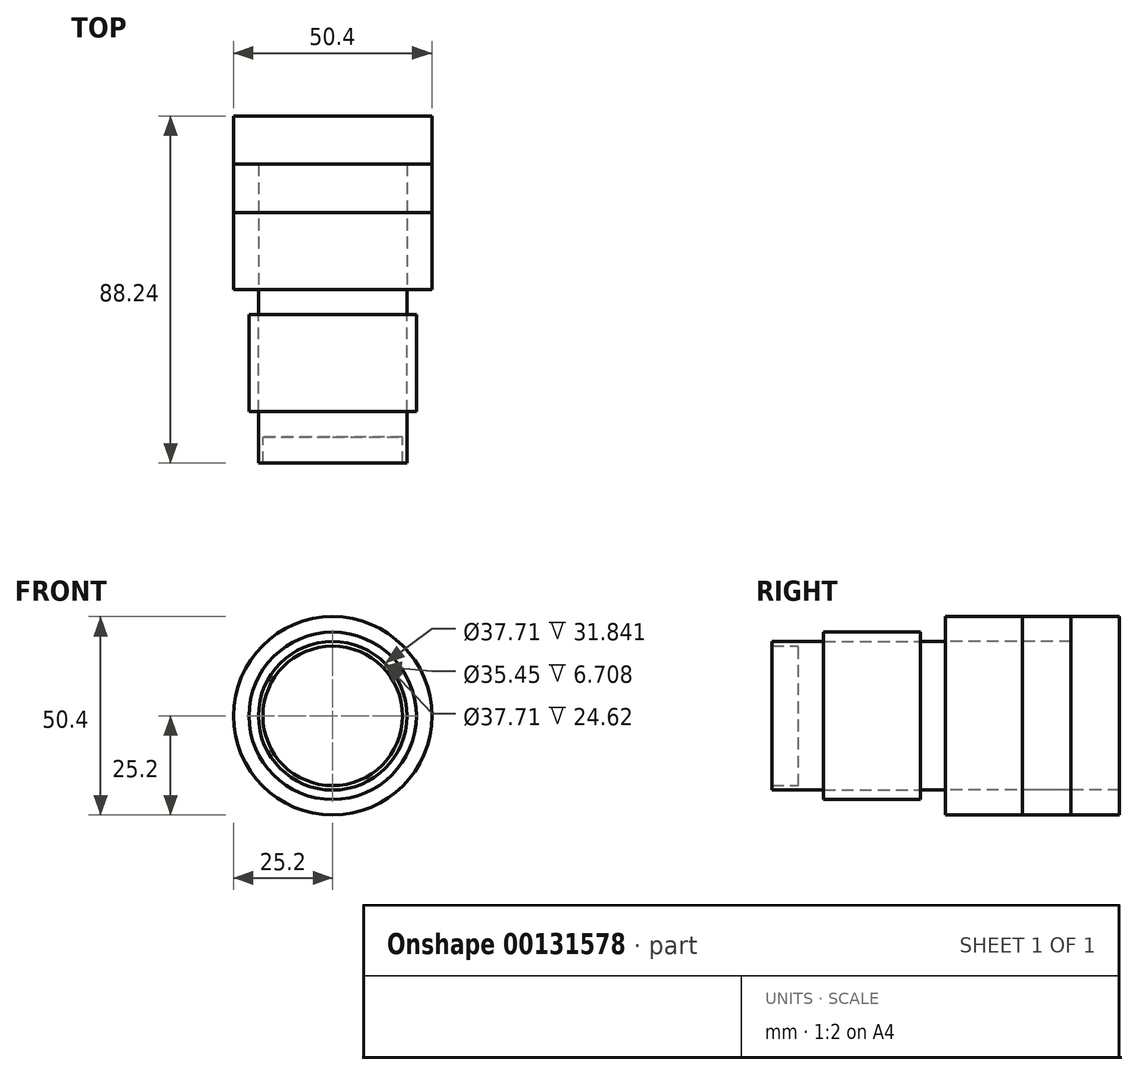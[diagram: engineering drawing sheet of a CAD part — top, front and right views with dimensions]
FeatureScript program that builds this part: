
annotation { "Feature Type Name" : "Feature", "Feature Type Description" : "" }
export const myFeature = defineFeature(function(context is Context, id is Id, definition is map)
    precondition{}
    {
        {
            var Q0;
            Q0=qCreatedBy(makeId("Front.planeOp"),FACE);
            var sketch = newSketch(context, id + "F0", { "sketchPlane" : qUnion([Q0])});
            skCircle(sketch, "E0", {"center": v(0, 0) * mm, "radius": 17.73 * mm});
            skCircle(sketch, "E1", {"center": v(0, 0) * mm, "radius": 18.85 * mm});
            skSolve(sketch);
        }
        {
            var Q0;
            Q0=makeQuery(id+"F0.imprint","IMPRINT",FACE,{"disambiguationData":[TD([[makeQuery(id+"F0.imprint","IMPRINT",EDGE,{"derivedFrom":sQuery(id+"F0.wireOp",EDGE,"E0")}),1.0]])]});
            var Q1;
            Q1=makeQuery(id+"F0.imprint","IMPRINT",FACE,{"disambiguationData":[TD([[makeQuery(id+"F0.imprint","IMPRINT",EDGE,{"derivedFrom":sQuery(id+"F0.wireOp",EDGE,"E0")}),-1.0]])]});
            extrude(context, id + "F1", {"entities" : qUnion([Q0, Q1]), "endBound" : BoundingType.SYMMETRIC, "depth" : 37.38 * mm});
        }
        {
            var Q0;
            Q0=makeQuery(id+"F0.imprint","IMPRINT",FACE,{"disambiguationData":[TD([[makeQuery(id+"F0.imprint","IMPRINT",EDGE,{"derivedFrom":sQuery(id+"F0.wireOp",EDGE,"E0")}),-1.0]])]});
            var Q1;
            Q1=makeQuery(id+"F1.opExtrude","CAP_FACE",FACE,{"disambiguationData":[OSD([sQuery(id+"F0.wireOp",EDGE,"E1")])],"isStart":true});
            extrude(context, id + "F2", {"entities" : qUnion([Q0, Q1]), "operationType" : NewBodyOperationType.ADD, "depth" : 25.4 * mm});
        }
        {
            var Q0;
            Q0=makeQuery(id+"F1.opExtrude","CAP_FACE",FACE,{"disambiguationData":[OSD([sQuery(id+"F0.wireOp",EDGE,"E1")])],"isStart":true});
            var sketch = newSketch(context, id + "F3", { "sketchPlane" : qUnion([Q0])});
            skCircle(sketch, "E2.0", {"center": v(0, 0) * mm, "radius": 25.2 * mm});
            skCircle(sketch, "E3.0", {"center": v(0, 0) * mm, "radius": 28.79 * mm});
            skCircle(sketch, "E4.0", {"center": v(0, 0) * mm, "radius": 35.36 * mm});
            skCircle(sketch, "E5.0", {"center": v(0, 0) * mm, "radius": 38.85 * mm});
            skSolve(sketch);
        }
        {
            var Q0;
            Q0=makeQuery(id+"F3.imprint","IMPRINT",FACE,{"disambiguationData":[TD([[makeQuery(id+"F3.imprint","IMPRINT",EDGE,{"derivedFrom":sQuery(id+"F3.wireOp",EDGE,"E2.0")}),1.0]])]});
            extrude(context, id + "F4", {"entities" : qUnion([Q0]), "depth" : 31.84 * mm});
        }
        {
            var Q0;
            Q0=qCreatedBy(makeId("Front.planeOp"),FACE);
            var sketch = newSketch(context, id + "F5", { "sketchPlane" : qUnion([Q0])});
            skCircle(sketch, "E6", {"center": v(0, 0) * mm, "radius": 21.26 * mm});
            skSolve(sketch);
        }
        {
            var Q0;
            Q0=makeQuery(id+"F5.imprint","IMPRINT",FACE,{"disambiguationData":[TD([[makeQuery(id+"F5.imprint","IMPRINT",EDGE,{"derivedFrom":sQuery(id+"F5.wireOp",EDGE,"E6")}),1.0]])]});
            var Q1;
            Q1=makeQuery(id+"F4.opExtrude","CAP_FACE",FACE,{"disambiguationData":[OSD([sQuery(id+"F0.wireOp",EDGE,"E1"),sQuery(id+"F3.wireOp",EDGE,"E2.0")])],"isStart":false});
            extrude(context, id + "F6", {"entities" : qUnion([Q0, Q1]), "endBound" : BoundingType.SYMMETRIC, "oppositeDirection" : true, "depth" : 24.62 * mm});
        }
    });
